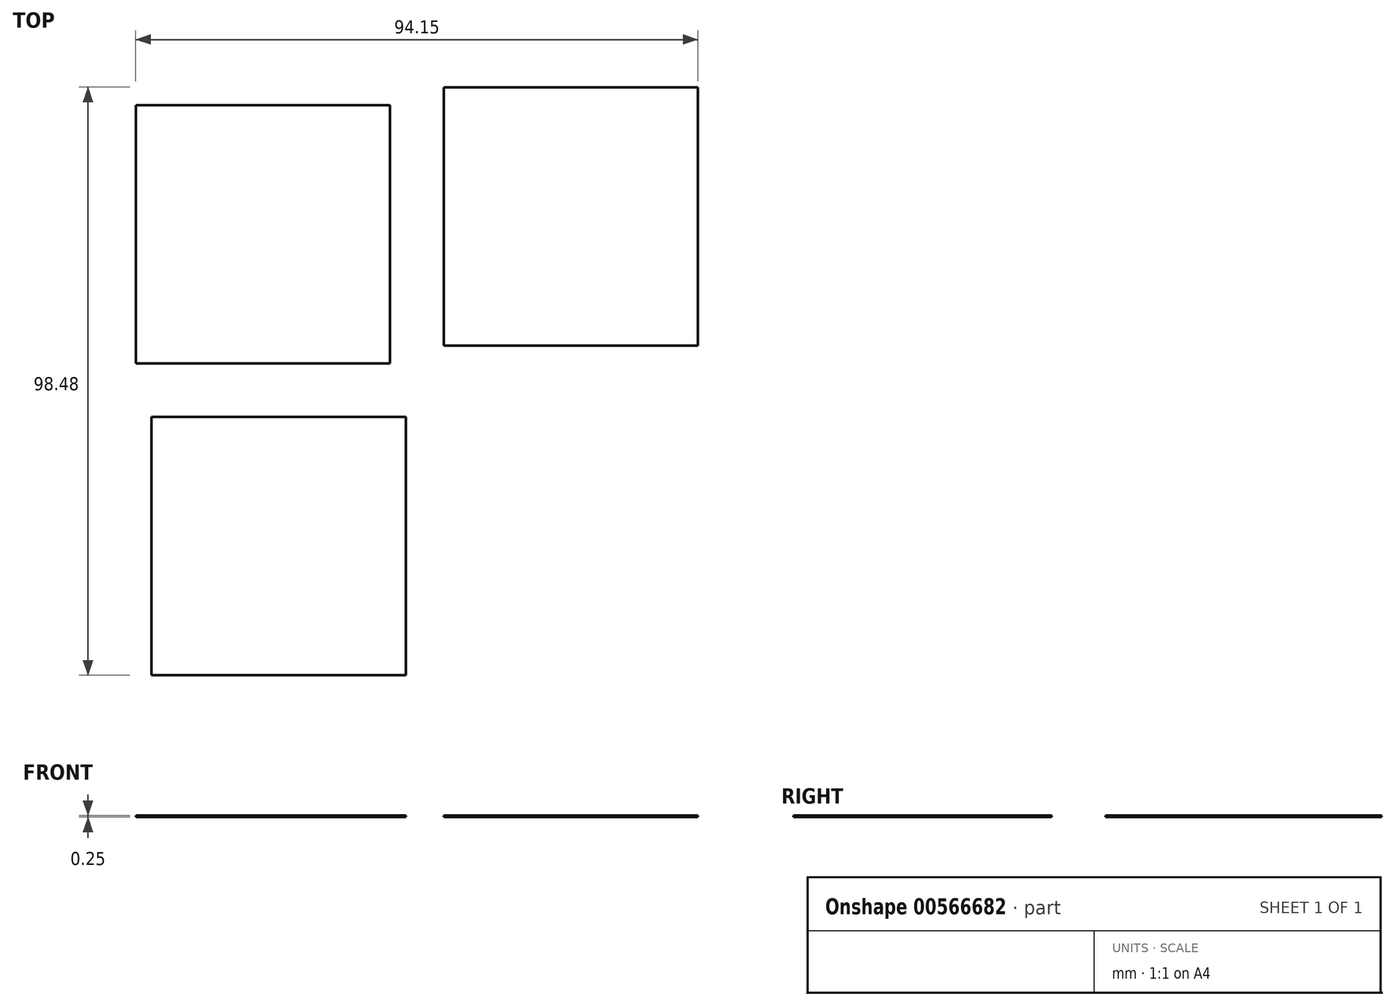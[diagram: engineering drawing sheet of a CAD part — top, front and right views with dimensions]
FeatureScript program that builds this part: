
annotation { "Feature Type Name" : "Feature", "Feature Type Description" : "" }
export const myFeature = defineFeature(function(context is Context, id is Id, definition is map)
    precondition{}
    {
        {
            var Q0;
            Q0=qCreatedBy(makeId("Top.planeOp"),FACE);
            var sketch = newSketch(context, id + "F0", { "sketchPlane" : qUnion([Q0])});
            skLineSegment(sketch, "E0.bottom", {"start": v(-13.47, 5.66) * mm, "end": v(-56.06, 5.66) * mm});
            skLineSegment(sketch, "E0.top", {"start": v(-13.47, 48.9) * mm, "end": v(-56.06, 48.9) * mm});
            skLineSegment(sketch, "E0.left", {"start": v(-13.47, 5.66) * mm, "end": v(-13.47, 48.9) * mm});
            skLineSegment(sketch, "E0.right", {"start": v(-56.06, 5.66) * mm, "end": v(-56.06, 48.9) * mm});
            skPoint(sketch, "E0.middle", {"position": v(-34.77, 27.28) * mm});
            skLineSegment(sketch, "E1.bottom", {"start": v(38.1, 8.65) * mm, "end": v(-4.5, 8.65) * mm});
            skLineSegment(sketch, "E1.top", {"start": v(38.1, 51.9) * mm, "end": v(-4.5, 51.9) * mm});
            skLineSegment(sketch, "E1.left", {"start": v(38.1, 8.65) * mm, "end": v(38.1, 51.9) * mm});
            skLineSegment(sketch, "E1.right", {"start": v(-4.5, 8.65) * mm, "end": v(-4.5, 51.9) * mm});
            skPoint(sketch, "E1.middle", {"position": v(16.8, 30.27) * mm});
            skLineSegment(sketch, "E2.bottom", {"start": v(-10.81, -46.58) * mm, "end": v(-53.4, -46.58) * mm});
            skLineSegment(sketch, "E2.top", {"start": v(-10.81, -3.33) * mm, "end": v(-53.4, -3.33) * mm});
            skLineSegment(sketch, "E2.left", {"start": v(-10.81, -46.58) * mm, "end": v(-10.81, -3.33) * mm});
            skLineSegment(sketch, "E2.right", {"start": v(-53.4, -46.58) * mm, "end": v(-53.4, -3.33) * mm});
            skPoint(sketch, "E2.middle", {"position": v(-32.1, -24.95) * mm});
            skSolve(sketch);
        }
        {
            var Q0;
            Q0=makeQuery(id+"F0.imprint","IMPRINT",FACE,{"disambiguationData":[TD([[makeQuery(id+"F0.imprint","IMPRINT",EDGE,{"derivedFrom":sQuery(id+"F0.wireOp",EDGE,"E0.bottom")}),-1.0]])]});
            extrude(context, id + "F1", {"entities" : qUnion([Q0]), "depth" : 0.25 * mm, "offsetDistance" : 25.4 * mm});
        }
        {
            var Q0;
            Q0 = qSketchRegion(id + "F0", true);
            extrude(context, id + "F2", {"entities" : qUnion([Q0]), "operationType" : NewBodyOperationType.ADD, "depth" : 0.25 * mm, "offsetDistance" : 25.4 * mm});
        }
    });
